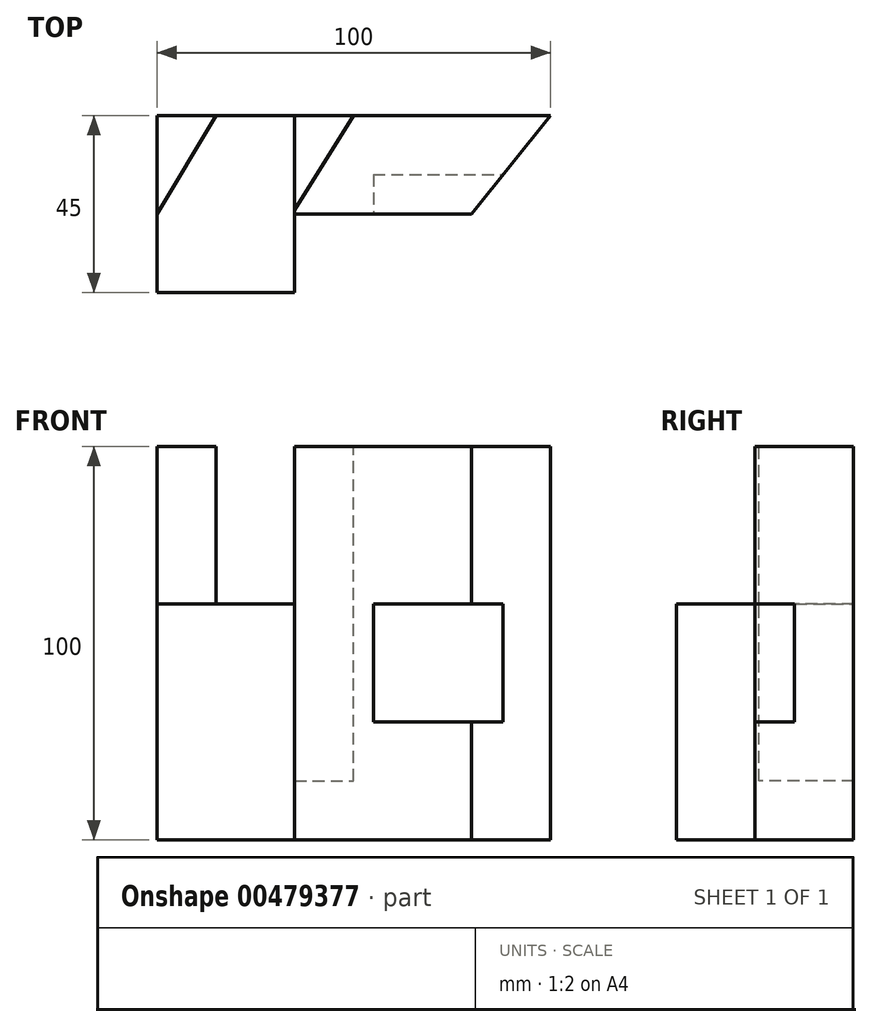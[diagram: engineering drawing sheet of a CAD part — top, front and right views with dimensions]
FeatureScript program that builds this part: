
annotation { "Feature Type Name" : "Feature", "Feature Type Description" : "" }
export const myFeature = defineFeature(function(context is Context, id is Id, definition is map)
    precondition{}
    {
        {
            var Q0;
            Q0=qCreatedBy(makeId("Top.planeOp"),FACE);
            var sketch = newSketch(context, id + "F0", { "sketchPlane" : qUnion([Q0])});
            skLineSegment(sketch, "E0", {"start": v(0, 0) * mm, "end": v(0, 45) * mm});
            skLineSegment(sketch, "E1", {"start": v(100, 45) * mm, "end": v(0, 45) * mm});
            skLineSegment(sketch, "E2", {"start": v(0, 0) * mm, "end": v(35, 0) * mm});
            skLineSegment(sketch, "E3", {"start": v(35, 0) * mm, "end": v(35, 20) * mm});
            skLineSegment(sketch, "E4", {"start": v(35, 20) * mm, "end": v(80, 20) * mm});
            skLineSegment(sketch, "E5", {"start": v(80, 20) * mm, "end": v(100, 45) * mm});
            skSolve(sketch);
        }
        {
            var Q0;
            Q0 = qSketchRegion(id + "F0", true);
            extrude(context, id + "F1", {"entities" : qUnion([Q0]), "depth" : 100 * mm});
        }
        {
            var Q0;
            Q0=makeQuery(id+"F1.opExtrude","CAP_FACE",FACE,{"disambiguationData":[OSD([sQuery(id+"F0.wireOp",EDGE,"E0"),sQuery(id+"F0.wireOp",EDGE,"E1"),sQuery(id+"F0.wireOp",EDGE,"E2"),sQuery(id+"F0.wireOp",EDGE,"E3"),sQuery(id+"F0.wireOp",EDGE,"E4"),sQuery(id+"F0.wireOp",EDGE,"E5")])],"isStart":false});
            var sketch = newSketch(context, id + "F2", { "sketchPlane" : qUnion([Q0])});
            skLineSegment(sketch, "E6", {"start": v(35, 0) * mm, "end": v(35, 45) * mm});
            skLineSegment(sketch, "E7", {"start": v(35, 45) * mm, "end": v(15, 45) * mm});
            skLineSegment(sketch, "E8", {"start": v(15, 45) * mm, "end": v(0, 20) * mm});
            skLineSegment(sketch, "E9", {"start": v(0, 20) * mm, "end": v(0, 0) * mm});
            skLineSegment(sketch, "E10", {"start": v(0, 0) * mm, "end": v(35, 0) * mm});
            skSolve(sketch);
        }
        {
            var Q0;
            Q0 = qSketchRegion(id + "F2", true);
            extrude(context, id + "F3", {"entities" : qUnion([Q0]), "operationType" : NewBodyOperationType.REMOVE, "oppositeDirection" : true, "depth" : 40 * mm});
        }
        {
            var Q0;
            Q0=qCreatedBy(makeId("Top.planeOp"),FACE);
            cPlane(context, id + "F4", {"entities" : qUnion([Q0]), "cplaneType" : CPlaneType.OFFSET, "offset" : 15 * mm, "width" : 150 * mm, "height" : 150 * mm});
        }
        {
            var Q0;
            {var subQ0=sQuery(id+"F0.wireOp",EDGE,"E1");var subQ1=sQuery(id+"F0.wireOp",EDGE,"E4");var subQ2=sQuery(id+"F0.wireOp",EDGE,"E5");Q0=makeQuery(id+"F3.boolean.opBoolean","SPLIT",FACE,{"disambiguationData":[TD([makeQuery(id+"F1.opExtrude","SWEPT_FACE",FACE,{"disambiguationData":[OSD([subQ1])]})])],"derivedFrom":makeQuery(id+"F1.opExtrude","CAP_FACE",FACE,{"disambiguationData":[OSD([sQuery(id+"F0.wireOp",EDGE,"E0"),subQ0,sQuery(id+"F0.wireOp",EDGE,"E2"),sQuery(id+"F0.wireOp",EDGE,"E3"),subQ1,subQ2])],"isStart":false})});}
            var sketch = newSketch(context, id + "F5", { "sketchPlane" : qUnion([Q0])});
            skLineSegment(sketch, "E11", {"start": v(35, 45) * mm, "end": v(35, 20) * mm});
            skLineSegment(sketch, "E12", {"start": v(35, 21) * mm, "end": v(50, 45) * mm});
            skLineSegment(sketch, "E13", {"start": v(50, 45) * mm, "end": v(35, 45) * mm});
            skSolve(sketch);
        }
        {
            var Q0;
            Q0 = qSketchRegion(id + "F5", true);
            var Q1;
            Q1=qCreatedBy(id+"F4.planeOp",FACE);
            extrude(context, id + "F6", {"entities" : qUnion([Q0]), "operationType" : NewBodyOperationType.REMOVE, "endBound" : BoundingType.UP_TO_SURFACE, "oppositeDirection" : true, "endBoundEntityFace" : qUnion([Q1]), "depth" : 85 * mm});
        }
        {
            var Q0;
            Q0=makeQuery(id+"F1.opExtrude","SWEPT_FACE",FACE,{"disambiguationData":[OSD([sQuery(id+"F0.wireOp",EDGE,"E4")])]});
            var sketch = newSketch(context, id + "F7", { "sketchPlane" : qUnion([Q0])});
            skLineSegment(sketch, "E14.bottom", {"start": v(55, 30) * mm, "end": v(94.07, 30) * mm});
            skLineSegment(sketch, "E14.top", {"start": v(55, 60) * mm, "end": v(94.07, 60) * mm});
            skLineSegment(sketch, "E14.left", {"start": v(55, 30) * mm, "end": v(55, 60) * mm});
            skLineSegment(sketch, "E14.right", {"start": v(94.07, 30) * mm, "end": v(94.07, 60) * mm});
            skSolve(sketch);
        }
        {
            var Q0;
            Q0 = qSketchRegion(id + "F7", true);
            extrude(context, id + "F8", {"entities" : qUnion([Q0]), "operationType" : NewBodyOperationType.REMOVE, "oppositeDirection" : true, "depth" : 10 * mm});
        }
    });
